# Revit family: 1313xxx Delphi Twin (UL)
name_source: partatom
category: Lighting Fixtures
revit_build: Autodesk Revit 2018 (Build: 20170223_1515(x64)
units: mm (PartAtom-declared; Revit-internal decimal feet)

## family parameters
Always vertical = Yes
Cut with Voids When Loaded = No
Host = Wall
Light Source = No
OmniClass Number = 23.80.70.00
OmniClass Title = Lighting
Part Type = Normal
Room Calculation Point = No
Round Connector Dimension = Use Diameter
Shared = No

## types (1)
- Astro Delphi Twin (UL)
    ADA compliant = Yes
    Dimmable = Yes
    Dimming Method = Lamp Dependent
    Driver Included = Not Applicable
    Driver Required = No
    Efficacy (lm/w) = Lamp Dependent
    Electrical Class = 1
    Lamp = Incandescent
    Light Source Fixed = No
    Location / IP Rating = Dry
    Main Finish = Polished Chrome
    Main Material = Metal - Mild Steel
    Manufacturer = Astro Lighting Ltd
    Manufacturer URL - Europe and Rest of World = www.astrolighting.com
    Manufacturer URL - North America = us.astrolighting.com
    Power (Watts) = Lamp Dependent
    Product CCT = Lamp Dependent
    Product CRI = Lamp Dependent
    Product Dimensions (in) = 11.10x4.25x5
    Product Location = Interior
    Product Name = Delphi Twin
    Product SKU = 1313003
    Product URL = https://us.astrolighting.com
    Product Weight (lb) = 2.734
    URL = www.astrolighting.com

## geometry (parser evidence)
native form markers: Sweep x2
no freeform markers — native parametric forms only
